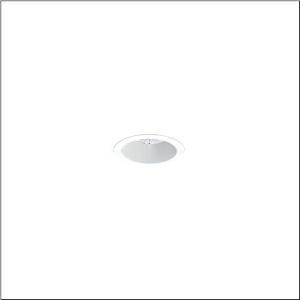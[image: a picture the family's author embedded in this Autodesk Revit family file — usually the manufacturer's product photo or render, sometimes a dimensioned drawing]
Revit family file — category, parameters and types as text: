
# Revit family: lunis_21_s_51db18ta91c
name_source: partatom
category: Lighting Fixtures
units: mm (PartAtom-declared; Revit-internal decimal feet)

## family parameters
Cut with Voids When Loaded = No
Host = Face
Light Source = No
Part Type = Normal
Room Calculation Point = No
Round Connector Dimension = Use Diameter
Shared = No

## types (1)
- --- (1 x LED 3000 K ... 6500 K, 1250 lm, 8 W, 4000K)
    Apparent Load = 8 VA
    CIE Flux Codes = 86 95 99 100 100
    Color Rendering = 80
    Color Temperature = 4000K
    Default Elevation = 1800 mm
    Description = Lunis 21 S, downlight, light control with lens, of PMMA, anti glare with reflector, of plastic, light emission: direct distribution, LED rated luminous flux: 1.250lm, light colour: 8tw, with terminal, 5-pole, mains connection: 220..240V, AC, 50..60Hz, housing, round, of diecast aluminium, traffic white (RAL 9016), diameter: 84mm, clamping range: 1..40mm, protection rating (complete): IP20, protection rating (on room side): IP54, insulation class (complete): insulation class II (safety insulation), certification: CE, impact resistance: IK03, packaging unit: 1 piece
    Height = 0 mm  [stored 0 ft]
    Lamp = 1 x LED 3000 K ... 6500 K
    Lamp Light Flux = 1250 lm
    Lamp Power = 8 W
    Lamp count = 1
    Length = 84 mm
    Luminous efficacy = 156 lm/W
    Manufacturer = Siteco
    ModVariant = No
    Model = 51DB18TA91C
    Mounting Place = Ceiling
    Mounting Type = Recessed
    Number of Poles = 1
    OnlyDefault = Yes
    Power Factor = 1
    Product Name = Lunis 21 S
    Product group = downlight
    ProductGroupID = 401
    Protection Class = Protection class II
    Protection Degree = IP 20
    RLX_Detail_Level = 1
    RLX_Emergency_Light_Flux = 0 lm
    RLX_Emergency_Type = 0
    RLX_Emergency_Type_DB = No
    RlxData = <blob elided: 7973 chars, md5=b2720a7f>
    Socket = socket
    Standby Power = 0 W
    System Light Flux = 1250 lm
    System Power = 8 W
    Type Comments = individual setting: CCT=4000K, colour temperature 4000K, luminous flux: 100 % | (OFF | OFF | ON | OFF) | 200 mA
    Type Image = l_1290842.jpg
    URL = http://relux.com
    VarID = @adj_035549
    Voltage = 0 V
    Weight = 0.00 kg
    Width = 0 mm  [stored 0 ft]

note: [stored X ft] marks values corroborated as IEEE doubles in the binary element streams (Revit-internal decimal feet)

## geometry (parser evidence)
native form markers: Sweep x8
no freeform markers — native parametric forms only
